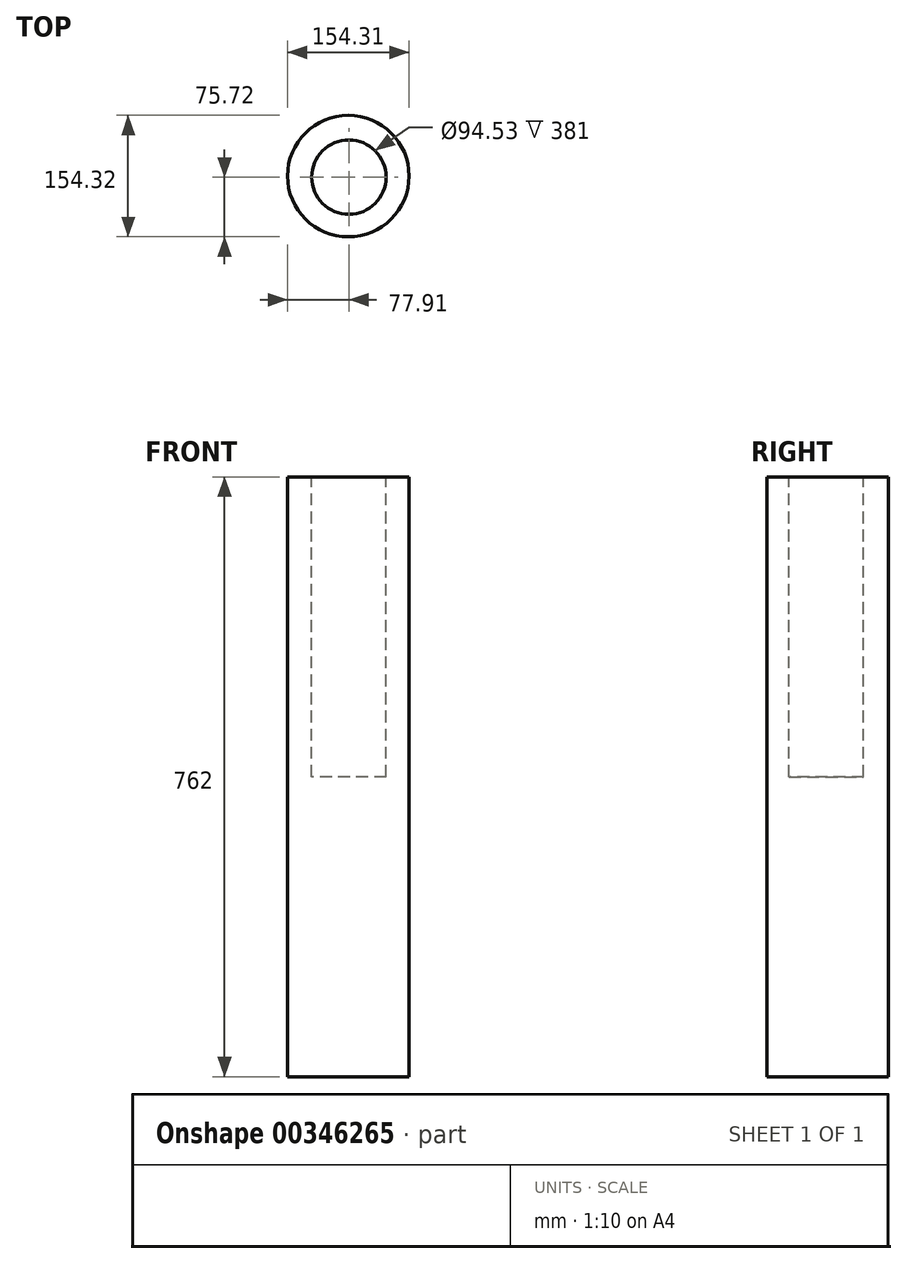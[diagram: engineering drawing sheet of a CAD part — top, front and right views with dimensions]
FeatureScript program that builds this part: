
annotation { "Feature Type Name" : "Feature", "Feature Type Description" : "" }
export const myFeature = defineFeature(function(context is Context, id is Id, definition is map)
    precondition{}
    {
        {
            var Q0;
            Q0=qCreatedBy(makeId("Top.planeOp"),FACE);
            var sketch = newSketch(context, id + "F0", { "sketchPlane" : qUnion([Q0])});
            skCircle(sketch, "E0", {"center": v(-0.75, 1.44) * mm, "radius": 77.16 * mm});
            skPoint(sketch, "E0.first.point", {"position": v(-76.57, -12.9) * mm});
            skPoint(sketch, "E0.second.point", {"position": v(75.85, 10.71) * mm});
            skPoint(sketch, "E0.third.point", {"position": v(5.22, -75.5) * mm});
            skSolve(sketch);
        }
        {
            var Q0;
            Q0=makeQuery(id+"F0.imprint","IMPRINT",FACE,{"disambiguationData":[TD([[makeQuery(id+"F0.imprint","IMPRINT",EDGE,{"derivedFrom":sQuery(id+"F0.wireOp",EDGE,"E0")}),1.0]])]});
            extrude(context, id + "F1", {"entities" : qUnion([Q0]), "depth" : 762 * mm});
        }
        {
            var Q0;
            Q0=makeQuery(id+"F1.opExtrude","CAP_FACE",FACE,{"disambiguationData":[OSD([sQuery(id+"F0.wireOp",EDGE,"E0")])],"isStart":false});
            var sketch = newSketch(context, id + "F2", { "sketchPlane" : qUnion([Q0])});
            skCircle(sketch, "E1", {"center": v(0, 0) * mm, "radius": 47.27 * mm});
            skSolve(sketch);
        }
        {
            var Q0;
            Q0 = qSketchRegion(id + "F2", true);
            extrude(context, id + "F3", {"entities" : qUnion([Q0]), "operationType" : NewBodyOperationType.REMOVE, "oppositeDirection" : true, "depth" : 381 * mm});
        }
    });
